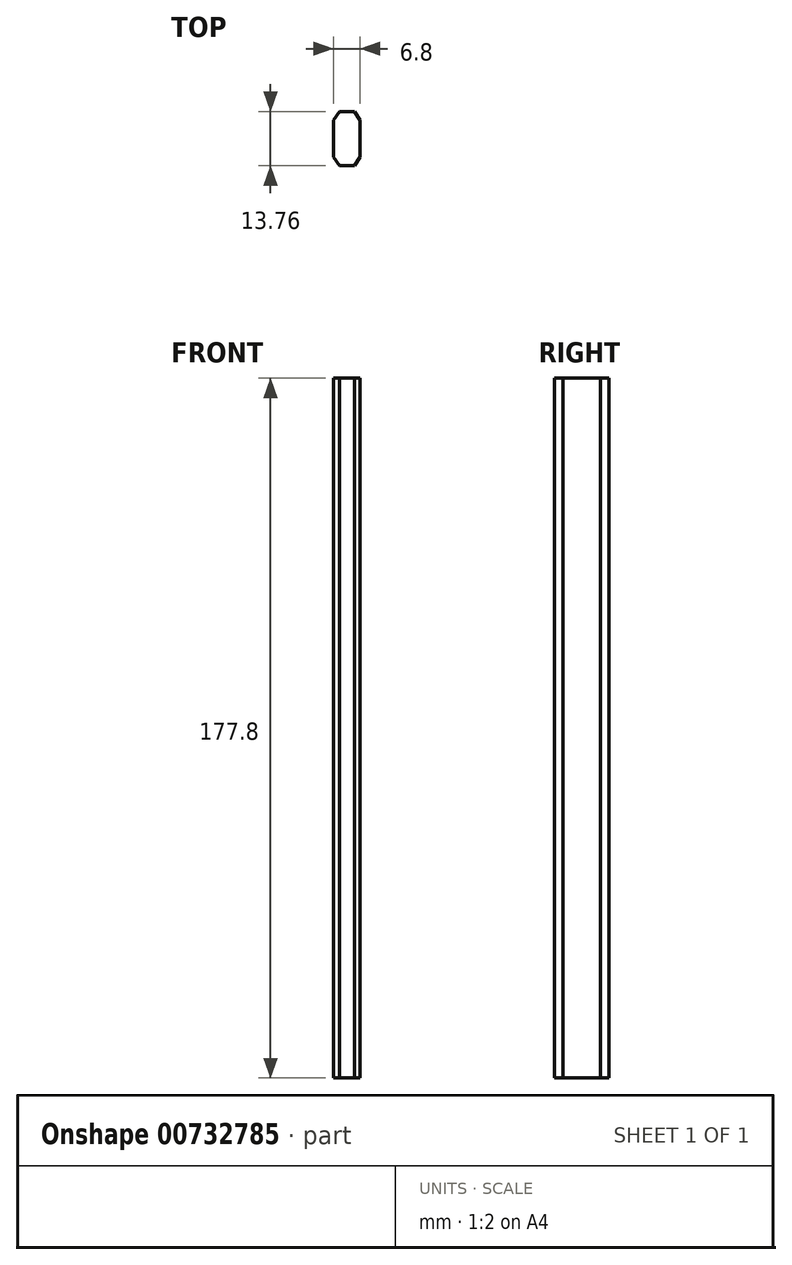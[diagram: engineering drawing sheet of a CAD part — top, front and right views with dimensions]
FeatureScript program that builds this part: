
annotation { "Feature Type Name" : "Feature", "Feature Type Description" : "" }
export const myFeature = defineFeature(function(context is Context, id is Id, definition is map)
    precondition{}
    {
        {
            var Q0;
            Q0=qCreatedBy(makeId("Top.planeOp"),FACE);
            var sketch = newSketch(context, id + "F0", { "sketchPlane" : qUnion([Q0])});
            skLineSegment(sketch, "E0", {"start": v(0, 0) * mm, "end": v(0, 6.88) * mm});
            skLineSegment(sketch, "E1", {"start": v(0, 6.88) * mm, "end": v(-1.9, 6.88) * mm});
            skLineSegment(sketch, "E2", {"start": v(-1.9, 6.88) * mm, "end": v(-3.4, 4.75) * mm});
            skLineSegment(sketch, "E3", {"start": v(-3.4, 4.75) * mm, "end": v(-3.4, 0) * mm});
            skLineSegment(sketch, "E4", {"start": v(-3.4, 0) * mm, "end": v(0, 0) * mm});
            skLineSegment(sketch, "E5.MirrorCS", {"start": v(0, 6.88) * mm, "end": v(1.9, 6.88) * mm});
            skLineSegment(sketch, "E6.MirrorCS", {"start": v(1.9, 6.88) * mm, "end": v(3.4, 4.75) * mm});
            skLineSegment(sketch, "E7.MirrorCS", {"start": v(3.4, 4.75) * mm, "end": v(3.4, 0) * mm});
            skLineSegment(sketch, "E8.MirrorCS", {"start": v(3.4, 0) * mm, "end": v(0, 0) * mm});
            skLineSegment(sketch, "E9", {"start": v(-3.4, 0) * mm, "end": v(3.4, 0) * mm});
            skLineSegment(sketch, "E10.MirrorCS", {"start": v(-3.4, -4.75) * mm, "end": v(-3.4, 0) * mm});
            skLineSegment(sketch, "E11.MirrorCS", {"start": v(-1.9, -6.88) * mm, "end": v(-3.4, -4.75) * mm});
            skLineSegment(sketch, "E12.MirrorCS", {"start": v(0, -6.88) * mm, "end": v(-1.9, -6.88) * mm});
            skLineSegment(sketch, "E13.MirrorCS", {"start": v(0, -6.88) * mm, "end": v(1.9, -6.88) * mm});
            skLineSegment(sketch, "E14.MirrorCS", {"start": v(1.9, -6.88) * mm, "end": v(3.4, -4.75) * mm});
            skLineSegment(sketch, "E15.MirrorCS", {"start": v(3.4, -4.75) * mm, "end": v(3.4, 0) * mm});
            skSolve(sketch);
        }
        {
            var Q0;
            {var subQ1=sQuery(id+"F0.wireOp",EDGE,"E0");Q0=makeQuery(id+"F0.imprint","IMPRINT",FACE,{"disambiguationData":[TD([[makeQuery(id+"F0.imprint","IMPRINT",EDGE,{"derivedFrom":subQ1}),1.0]])]});}
            var Q1;
            {var subQ1=sQuery(id+"F0.wireOp",EDGE,"E0");Q1=makeQuery(id+"F0.imprint","IMPRINT",FACE,{"disambiguationData":[TD([[makeQuery(id+"F0.imprint","IMPRINT",EDGE,{"derivedFrom":subQ1}),-1.0]])]});}
            var Q2;
            {var subQ0=sQuery(id+"F0.wireOp",EDGE,"E10.MirrorCS");Q2=makeQuery(id+"F0.imprint","IMPRINT",FACE,{"disambiguationData":[TD([[makeQuery(id+"F0.imprint","IMPRINT",EDGE,{"derivedFrom":subQ0}),-1.0]])]});}
            extrude(context, id + "F1", {"entities" : qUnion([Q0, Q1, Q2]), "depth" : 177.8 * mm, "offsetDistance" : 25 * mm});
        }
    });
